# Revit family: Toilet_Partition-Bobrick-B1086-Floor_To_Ceiling_Anchored
name_source: partatom
category: Specialty Equipment
revit_build: Autodesk Revit Architecture 2012 (Build: 20110916_2132(x64)
units: mm (PartAtom-declared; Revit-internal decimal feet)

## types (1)
- B-1086
    ADA Compliant = Yes
    Assembly Code = C1030200
    Description = Water and Fire-Resistant Solid Phenolic Partitions and Screens
    Door Panel = Yes
    DoorPanel Width = 24"
    Inswing = Yes
    Inswing Value = 24"
    Inswing Visibility = Yes
    Left Stile Value = 12"
    Left Stile Visible = Yes
    Left Stile Width = 12"
    Manufacturer = Bobrick Washroom Equipment, Inc.
    Model = B1086 DuraLineSeries Floor-to-Ceiling-Anchored
    Outswing = No
    Outswing Value = 25"
    Panel = No
    Panel Value = 24"
    Partition Material = Laminated Plastic - Bobrick - Designer White
    Right Stile Value = 12"
    Right Stile Visible = Yes
    Right Stile Width = 12"
    URL = http://www.bobrick.com
    Width Value = 24"

## geometry (parser evidence)
native form markers: Blend x8, Sweep x1
no freeform markers — native parametric forms only
